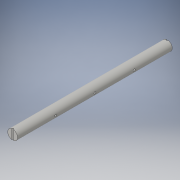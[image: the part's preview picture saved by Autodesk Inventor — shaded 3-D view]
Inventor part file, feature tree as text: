
AUTODESK INVENTOR PART (.ipt)
format: ipt  version: 2016 (Build 200138000, 138)  size: 135,680 bytes
history: native  units: in
note: dims shown in document units (in); Inventor stores cm internally (conversion verified against a paired STEP export)
features: extrude x4, sketch x3
ambient origin geometry x8: Origin, YZ Plane, XZ Plane, XY Plane, X Axis, Y Axis, Z Axis, Center Point
bodies: Solid1 (feature_tree)
feature tree (7):
  extrude  "Extrusion1"  Depth=8.0in TaperAngle=0.0deg
  extrude  "Extrusion4"  Depth=0.06in
  extrude  "Extrusion6"  Depth=2.0in TaperAngle=0.0deg
  extrude  "Extrusion8"  Depth=2.0in
  sketch  "Sketch1"  dims[d0=0.5in d1=8.0in d2=0.0in]
  sketch  "Sketch4"  dims[d13=0.06in d15=0.06in]
  sketch  "Sketch7"  dims[d16=0.1in d17=0.6in d18=0.0in d19=0.1in d20=0.06in d21=0.05in d26=0.5in d27=0.06in d28=1.0in d29=0.0in d42=2.0in d43=0.1in d44=2.0in d45=0.1in d46=2.0in d47=0.1in d48=1.0in d49=0.0in]
